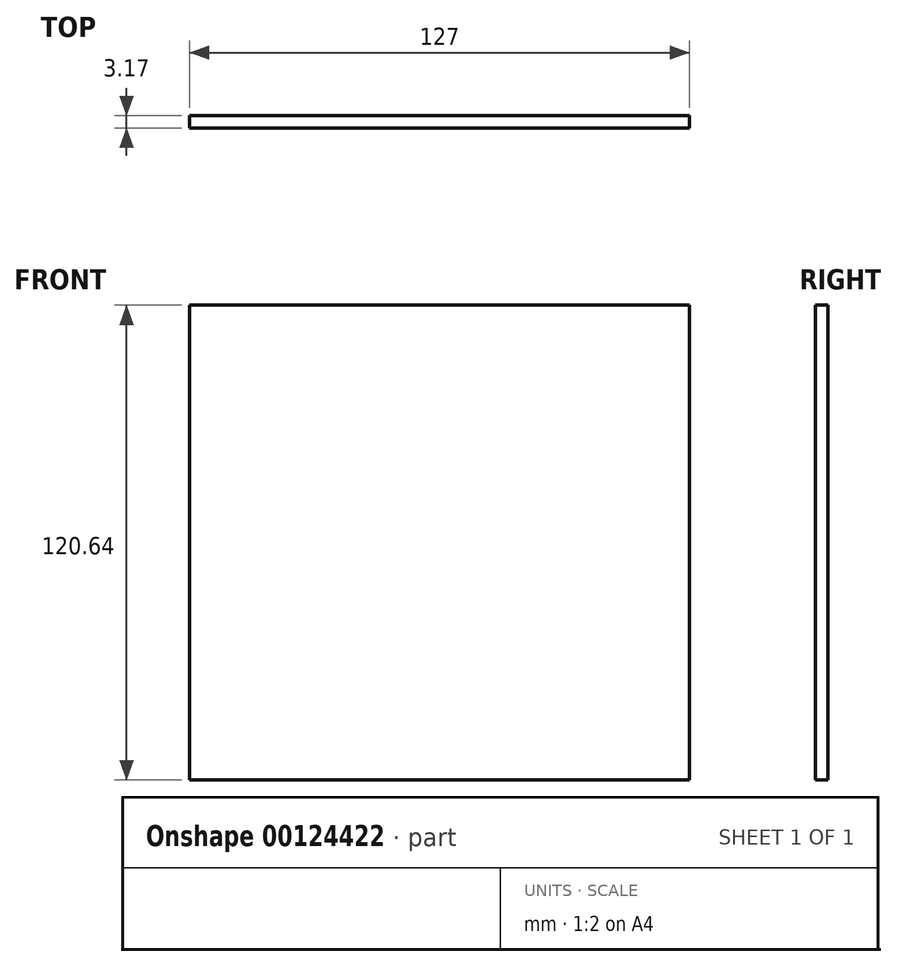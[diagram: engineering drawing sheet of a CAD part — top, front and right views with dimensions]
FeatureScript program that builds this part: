
annotation { "Feature Type Name" : "Feature", "Feature Type Description" : "" }
export const myFeature = defineFeature(function(context is Context, id is Id, definition is map)
    precondition{}
    {
        {
            var Q0;
            Q0=qCreatedBy(makeId("Front.planeOp"),FACE);
            var sketch = newSketch(context, id + "F0", { "sketchPlane" : qUnion([Q0])});
            skLineSegment(sketch, "E0.bottom", {"start": v(63.5, -60.33) * mm, "end": v(-63.5, -60.33) * mm});
            skLineSegment(sketch, "E0.top", {"start": v(63.5, 60.33) * mm, "end": v(-63.5, 60.33) * mm});
            skLineSegment(sketch, "E0.left", {"start": v(63.5, -60.33) * mm, "end": v(63.5, 60.32) * mm});
            skLineSegment(sketch, "E0.right", {"start": v(-63.5, -60.33) * mm, "end": v(-63.5, 60.32) * mm});
            skPoint(sketch, "E0.middle", {"position": v(0, 0) * mm});
            skSolve(sketch);
        }
        {
            var Q0;
            Q0 = qSketchRegion(id + "F0", true);
            extrude(context, id + "F1", {"entities" : qUnion([Q0]), "depth" : 3.17 * mm});
        }
    });
